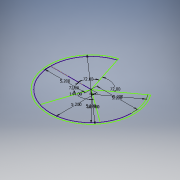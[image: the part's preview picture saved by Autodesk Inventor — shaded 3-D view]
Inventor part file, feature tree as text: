
AUTODESK INVENTOR PART (.ipt)
format: ipt  version: 2017 (Build 210142000, 142)  size: 98,304 bytes
history: native  units: in
note: dims shown in document units (in); Inventor stores cm internally (conversion verified against a paired STEP export)
features: sketch x1
ambient origin geometry x8: Origin, YZ Plane, XZ Plane, XY Plane, X Axis, Y Axis, Z Axis, Center Point
feature tree (1):
  sketch  "Sketch1"  dims[d0=5.2in d1=5.2in d2=5.2in d3=5.2in d4=5.2in d6=0.4947in d8=0.9895in d9=10.9in d10=0.4947in d11=0.4947in]
